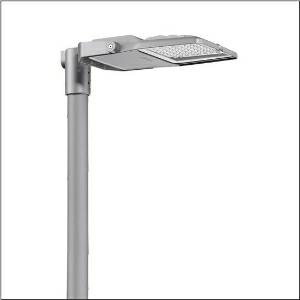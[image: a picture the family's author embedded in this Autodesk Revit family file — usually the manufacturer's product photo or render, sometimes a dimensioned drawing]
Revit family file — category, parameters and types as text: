
# Revit family: floodlight_fl_21_mini___pl64_5xa7775d2e3a_010e
name_source: partatom
category: Lighting Fixtures
units: mm (PartAtom-declared; Revit-internal decimal feet)

## family parameters
Cut with Voids When Loaded = No
Host = Face
Light Source = No
Part Type = Normal
Room Calculation Point = No
Round Connector Dimension = Use Diameter
Shared = No

## types (1)
- --- (1 x LED, 17220 lm, 142.9 W, 3000K)
    Apparent Load = 143 VA
    CIE Flux Codes = 28 80 98 100 100
    Color Rendering = 70
    Color Temperature = 3000K
    Default Elevation = 1800 mm
    Description = Floodlight FL 21 mini, floodlight, primary light control with lens, of PMMA, primary optical cover: protective disc, of toughened safety glass, transparent, light distribution: PL64, light emission: direct distribution, installation type: surface-mounted, LED, High Power LED, rated luminous flux: 17.220lm, luminous efficacy: 121lm/W, light colour: 730, colour temperature: 3000K, control gear: Smart Interface (Zhaga), control: flexible luminous flux parameterisation, time-dependent luminous flux control, constant luminous flux control, overheat protection, pre-setting: logarithmic dimming characteristic, with terminal, 6-pole, mains connection: 220..240V, AC, 50/60Hz, start of lifetime: 143W, end of service life: 151W, reduction: 63W, luminaire housing, of diecast aluminium, powder-coated, SITECO metallic grey (DB 702S), corrosivity category C5 mid according to DIN EN ISO 12944, suitable for swimming pools, chlorine-resistant, sealing non-destructively replaceable, please order mast flange separately, mast bracket, of steel, galvanised, powder-coated, SITECO metallic grey (DB 702S), Smart Interface above, protection rating (complete): IP66, insulation class (complete): insulation class II (safety insulation), certification: CE, ENEC, VDE, protection symbol: D, impact resistance: IK08, permissible operating ambient temperature: -40..+40°C, permissible operating ambient temperature for outdoor applications: -40..+50°C, standard: DIN EN 12944, LABS conformity tested according to VDMA 24364:2018-05, packaging unit: 1 piece

Light Distribution: PL64
    Height = 70 mm
    Lamp = 1 x LED
    Lamp Light Flux = 17220 lm
    Lamp Power = 142.9 W
    Lamp count = 1
    Length = 485 mm
    Luminous efficacy = 121 lm/W
    Manufacturer = Siteco
    ModVariant = No
    Model = 5XA7775D2E3A
    Number of Poles = 1
    OnlyDefault = Yes
    Power Factor = 1
    Product Name = Floodlight FL 21 mini | PL64
    Product group = floodlight | pylon annexe
    ProductGroupID = 6201
    Protection Class = Protection class II
    Protection Degree = IP 66
    RLX_Detail_Level = 1
    RLX_Emergency_Light_Flux = 0 lm
    RLX_Emergency_Type = 0
    RLX_Emergency_Type_DB = No
    RlxData = <blob elided: 101317 chars, md5=23e227d4>
    Socket = socket
    Standby Power = 0 W
    System Light Flux = 17220 lm
    System Power = 143 W
    Type Comments = factory setting: luminous flux: 100 % | dim-lin: 254 | 730 mA
    Type Image = l_1007125.jpg
    URL = http://relux.com
    VarID = @adj_164745
    Voltage = 0 V
    Weight = 0.00 kg
    Width = 337 mm

## geometry (parser evidence)
native form markers: Blend x4, Sweep x10
no freeform markers — native parametric forms only
